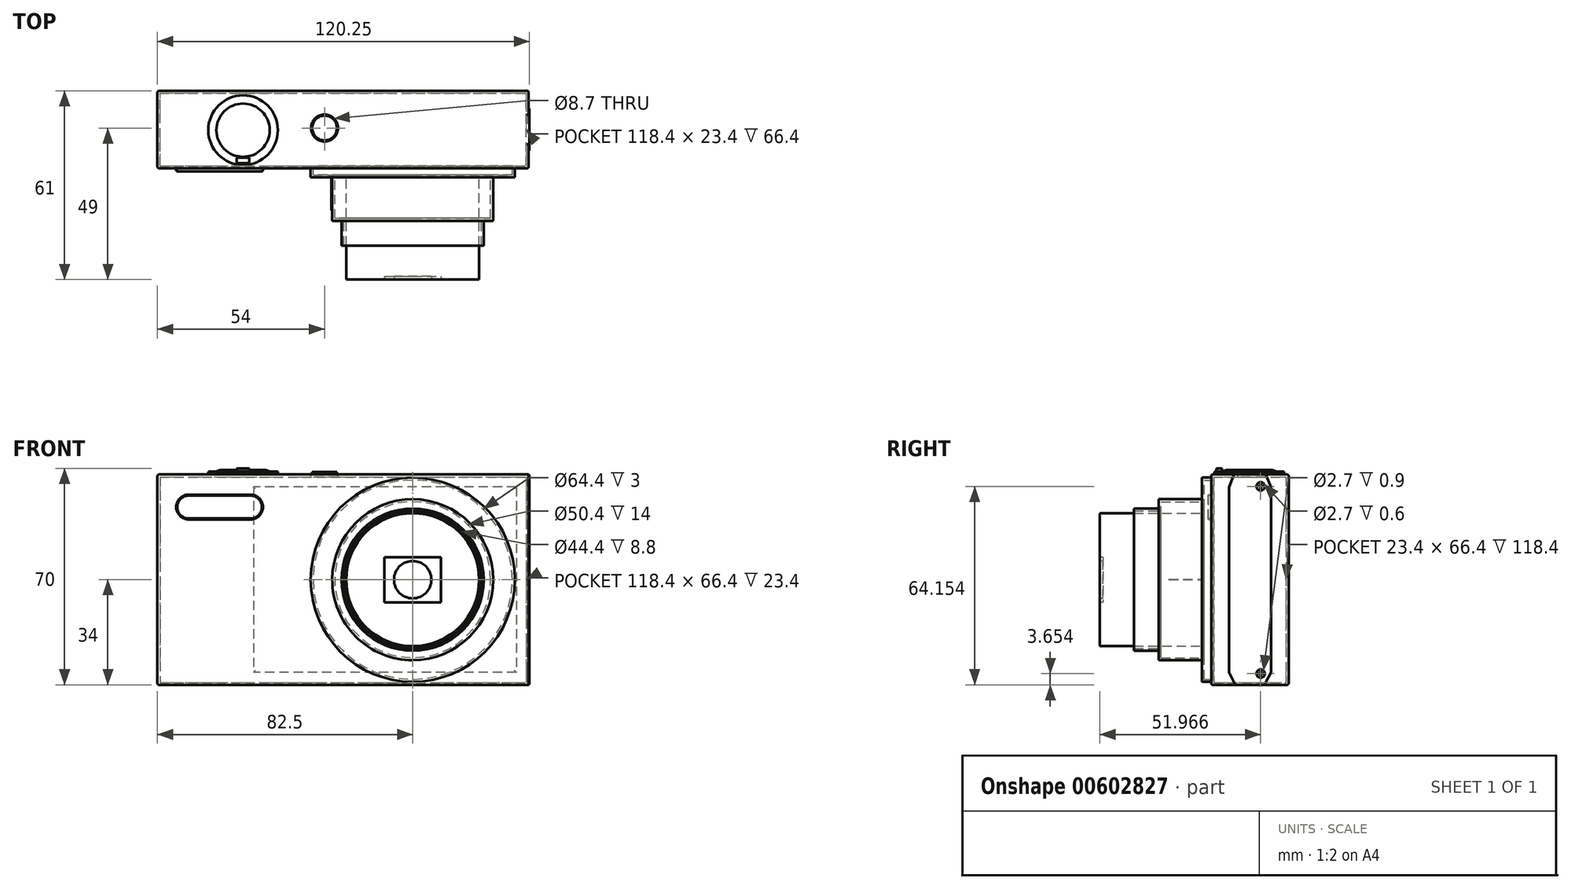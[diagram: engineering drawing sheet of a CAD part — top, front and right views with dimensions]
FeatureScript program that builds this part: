
annotation { "Feature Type Name" : "Feature", "Feature Type Description" : "" }
export const myFeature = defineFeature(function(context is Context, id is Id, definition is map)
    precondition{}
    {
        {
            var Q0;
            Q0=qCreatedBy(makeId("Front.planeOp"),FACE);
            var sketch = newSketch(context, id + "F0", { "sketchPlane" : qUnion([Q0])});
            skLineSegment(sketch, "E0.bottom", {"start": v(-60, 34) * mm, "end": v(60, 34) * mm});
            skLineSegment(sketch, "E0.top", {"start": v(-60, -34) * mm, "end": v(60, -34) * mm});
            skLineSegment(sketch, "E0.left", {"start": v(-60, 34) * mm, "end": v(-60, -34) * mm});
            skLineSegment(sketch, "E0.right", {"start": v(60, 34) * mm, "end": v(60, -34) * mm});
            skPoint(sketch, "E0.middle", {"position": v(0, 0) * mm});
            skCircle(sketch, "E1", {"center": v(22.5, 0) * mm, "radius": 33 * mm});
            skSolve(sketch);
        }
        {
            var Q0;
            Q0=makeQuery(id+"F0.imprint","IMPRINT",FACE,{"disambiguationData":[TD([[makeQuery(id+"F0.imprint","IMPRINT",EDGE,{"derivedFrom":sQuery(id+"F0.wireOp",EDGE,"E1")}),1.0]])]});
            extrude(context, id + "F1", {"entities" : qUnion([Q0]), "depth" : 28 * mm, "offsetDistance" : 25 * mm});
        }
        {
            var Q0;
            Q0=makeQuery(id+"F0.imprint","IMPRINT",FACE,{"disambiguationData":[TD([[makeQuery(id+"F0.imprint","IMPRINT",EDGE,{"derivedFrom":sQuery(id+"F0.wireOp",EDGE,"E0.bottom")}),-1.0]])]});
            extrude(context, id + "F2", {"entities" : qUnion([Q0]), "operationType" : NewBodyOperationType.ADD, "depth" : 25 * mm, "offsetDistance" : 25 * mm});
        }
        {
            var Q0;
            Q0=makeQuery(id+"F1.opExtrude","CAP_FACE",FACE,{"disambiguationData":[OSD([sQuery(id+"F0.wireOp",EDGE,"E1")])],"isStart":false});
            var sketch = newSketch(context, id + "F3", { "sketchPlane" : qUnion([Q0])});
            skCircle(sketch, "E2", {"center": v(22.5, 0) * mm, "radius": 26 * mm});
            skSolve(sketch);
        }
        {
            var Q0;
            Q0=makeQuery(id+"F3.imprint","IMPRINT",FACE,{"disambiguationData":[TD([[makeQuery(id+"F3.imprint","IMPRINT",EDGE,{"derivedFrom":sQuery(id+"F3.wireOp",EDGE,"E2")}),1.0]])]});
            var Q1;
            Q1=sQuery(id+"F3.wireOp",EDGE,"E2");
            extrude(context, id + "F4", {"entities" : qUnion([Q0]), "operationType" : NewBodyOperationType.ADD, "surfaceEntities" : qUnion([Q1]), "depth" : 14 * mm, "offsetDistance" : 25 * mm});
        }
        {
            var Q0;
            Q0=makeQuery(id+"F4.opExtrude","CAP_FACE",FACE,{"disambiguationData":[OSD([sQuery(id+"F3.wireOp",EDGE,"E2")])],"isStart":false});
            var sketch = newSketch(context, id + "F5", { "sketchPlane" : qUnion([Q0])});
            skCircle(sketch, "E3", {"center": v(22.5, 0) * mm, "radius": 23 * mm});
            skSolve(sketch);
        }
        {
            var Q0;
            Q0=makeQuery(id+"F5.imprint","IMPRINT",FACE,{"disambiguationData":[TD([[makeQuery(id+"F5.imprint","IMPRINT",EDGE,{"derivedFrom":sQuery(id+"F5.wireOp",EDGE,"E3")}),1.0]])]});
            extrude(context, id + "F6", {"entities" : qUnion([Q0]), "operationType" : NewBodyOperationType.ADD, "depth" : 8 * mm, "offsetDistance" : 25 * mm});
        }
        {
            var Q0;
            Q0=makeQuery(id+"F6.opExtrude","CAP_FACE",FACE,{"disambiguationData":[OSD([sQuery(id+"F5.wireOp",EDGE,"E3")])],"isStart":false});
            shell(context, id + "F7", {"entities" : qUnion([Q0]), "thickness" : 0.8 * mm});
        }
        {
            var Q0;
            Q0=qCreatedBy(makeId("Front.planeOp"),FACE);
            cPlane(context, id + "F8", {"entities" : qUnion([Q0]), "cplaneType" : CPlaneType.OFFSET, "offset" : 28 * mm, "width" : 150 * mm, "height" : 150 * mm});
        }
        {
            var Q0;
            Q0=qCreatedBy(id+"F8.planeOp",FACE);
            var sketch = newSketch(context, id + "F9", { "sketchPlane" : qUnion([Q0])});
            skCircle(sketch, "E4", {"center": v(22.5, 0) * mm, "radius": 21.5 * mm});
            skSolve(sketch);
        }
        {
            var Q0;
            Q0=makeQuery(id+"F9.imprint","IMPRINT",FACE,{"disambiguationData":[TD([[makeQuery(id+"F9.imprint","IMPRINT",EDGE,{"derivedFrom":sQuery(id+"F9.wireOp",EDGE,"E4")}),1.0]])]});
            extrude(context, id + "F10", {"entities" : qUnion([Q0]), "operationType" : NewBodyOperationType.ADD, "depth" : 33 * mm, "offsetDistance" : 25 * mm});
        }
        {
            var Q0;
            Q0=makeQuery(id+"F10.opExtrude","CAP_FACE",FACE,{"disambiguationData":[OSD([sQuery(id+"F9.wireOp",EDGE,"E4")])],"isStart":false});
            var sketch = newSketch(context, id + "F11", { "sketchPlane" : qUnion([Q0])});
            skLineSegment(sketch, "E5.bottom", {"start": v(13.35, 7.3) * mm, "end": v(31.65, 7.3) * mm});
            skLineSegment(sketch, "E5.top", {"start": v(13.35, -7.3) * mm, "end": v(31.65, -7.3) * mm});
            skLineSegment(sketch, "E5.left", {"start": v(13.35, 7.3) * mm, "end": v(13.35, -7.3) * mm});
            skLineSegment(sketch, "E5.right", {"start": v(31.65, 7.3) * mm, "end": v(31.65, -7.3) * mm});
            skPoint(sketch, "E5.middle", {"position": v(22.5, 0) * mm});
            skCircle(sketch, "E6", {"center": v(22.5, 0) * mm, "radius": 6.04 * mm});
            skSolve(sketch);
        }
        {
            var Q0;
            Q0=makeQuery(id+"F2.opExtrude","SWEPT_FACE",FACE,{"disambiguationData":[OSD([sQuery(id+"F0.wireOp",EDGE,"E0.bottom")])]});
            var sketch = newSketch(context, id + "F12", { "sketchPlane" : qUnion([Q0])});
            skCircle(sketch, "E7", {"center": v(-6, -12) * mm, "radius": 4 * mm});
            skCircle(sketch, "E8", {"center": v(-32.34, -12.7) * mm, "radius": 11.25 * mm});
            skCircle(sketch, "E9", {"center": v(-32.34, -12.7) * mm, "radius": 8.61 * mm});
            skPoint(sketch, "E10", {"position": v(-32.34, -22.45) * mm});
            skLineSegment(sketch, "E11.bottom", {"start": v(-30.34, -23.35) * mm, "end": v(-34.35, -23.35) * mm});
            skLineSegment(sketch, "E11.top", {"start": v(-30.34, -21.56) * mm, "end": v(-34.35, -21.56) * mm});
            skLineSegment(sketch, "E11.left", {"start": v(-30.34, -23.35) * mm, "end": v(-30.34, -21.56) * mm});
            skLineSegment(sketch, "E11.right", {"start": v(-34.35, -23.35) * mm, "end": v(-34.35, -21.56) * mm});
            skSolve(sketch);
        }
        {
            var Q0;
            Q0=makeQuery(id+"F12.imprint","IMPRINT",FACE,{"disambiguationData":[TD([[makeQuery(id+"F12.imprint","IMPRINT",EDGE,{"derivedFrom":sQuery(id+"F12.wireOp",EDGE,"E7")}),1.0]])]});
            extrude(context, id + "F13", {"entities" : qUnion([Q0]), "operationType" : NewBodyOperationType.ADD, "depth" : 0.75 * mm, "offsetDistance" : 25 * mm});
        }
        {
            var Q0;
            Q0=makeQuery(id+"F12.imprint","IMPRINT",FACE,{"disambiguationData":[TD([[makeQuery(id+"F12.imprint","IMPRINT",EDGE,{"derivedFrom":sQuery(id+"F12.wireOp",EDGE,"E11.bottom")}),-1.0]])]});
            extrude(context, id + "F14", {"entities" : qUnion([Q0]), "operationType" : NewBodyOperationType.ADD, "depth" : 2 * mm, "offsetDistance" : 25 * mm});
        }
        {
            var Q0;
            Q0=makeQuery(id+"F12.imprint","IMPRINT",FACE,{"disambiguationData":[TD([[makeQuery(id+"F12.imprint","IMPRINT",EDGE,{"derivedFrom":sQuery(id+"F12.wireOp",EDGE,"E8")}),1.0]])]});
            extrude(context, id + "F15", {"entities" : qUnion([Q0]), "operationType" : NewBodyOperationType.ADD, "depth" : 1 * mm, "offsetDistance" : 25 * mm});
        }
        {
            var Q0;
            Q0=makeQuery(id+"F12.imprint","IMPRINT",FACE,{"disambiguationData":[TD([[makeQuery(id+"F12.imprint","IMPRINT",EDGE,{"derivedFrom":sQuery(id+"F12.wireOp",EDGE,"E9")}),1.0]])]});
            extrude(context, id + "F16", {"entities" : qUnion([Q0]), "operationType" : NewBodyOperationType.ADD, "depth" : 1.5 * mm, "offsetDistance" : 25 * mm});
        }
        {
            var Q0;
            Q0=makeQuery(id+"F14.opExtrude","CAP_EDGE",EDGE,{"disambiguationData":[OSD([sQuery(id+"F12.wireOp",EDGE,"E11.bottom")])],"isStart":false});
            var Q1;
            Q1=makeQuery(id+"F14.opExtrude","CAP_EDGE",EDGE,{"disambiguationData":[OSD([sQuery(id+"F12.wireOp",EDGE,"E11.left")])],"isStart":false});
            var Q2;
            Q2=makeQuery(id+"F14.opExtrude","SWEPT_EDGE",EDGE,{"disambiguationData":[OSD([sQuery(id+"F12.wireOp",EDGE,"E11.bottom"),sQuery(id+"F12.wireOp",EDGE,"E11.left")])]});
            var Q3;
            Q3=makeQuery(id+"F14.opExtrude","CAP_EDGE",EDGE,{"disambiguationData":[OSD([sQuery(id+"F12.wireOp",EDGE,"E11.top")])],"isStart":false});
            var Q4;
            Q4=makeQuery(id+"F14.opExtrude","CAP_EDGE",EDGE,{"disambiguationData":[OSD([sQuery(id+"F12.wireOp",EDGE,"E11.right")])],"isStart":false});
            var Q5;
            Q5=makeQuery(id+"F14.opExtrude","SWEPT_EDGE",EDGE,{"disambiguationData":[OSD([sQuery(id+"F12.wireOp",EDGE,"E11.top"),sQuery(id+"F12.wireOp",EDGE,"E11.right")])]});
            var Q6;
            Q6=makeQuery(id+"F14.opExtrude","SWEPT_EDGE",EDGE,{"disambiguationData":[OSD([sQuery(id+"F12.wireOp",EDGE,"E11.top"),sQuery(id+"F12.wireOp",EDGE,"E11.left")])]});
            var Q7;
            Q7=makeQuery(id+"F14.opExtrude","SWEPT_EDGE",EDGE,{"disambiguationData":[OSD([sQuery(id+"F12.wireOp",EDGE,"E11.bottom"),sQuery(id+"F12.wireOp",EDGE,"E11.right")])]});
            var Q8;
            Q8=makeQuery(id+"F15.opExtrude","CAP_EDGE",EDGE,{"disambiguationData":[OSD([sQuery(id+"F12.wireOp",EDGE,"E11.bottom")])],"isStart":false});
            var Q9;
            Q9=makeQuery(id+"F15.opExtrude","CAP_EDGE",EDGE,{"disambiguationData":[OSD([sQuery(id+"F12.wireOp",EDGE,"E11.right")])],"isStart":false});
            fillet(context, id + "F17", {"entities" : qUnion([Q0, Q1, Q2, Q3, Q4, Q5, Q6, Q7, Q8, Q9]), "radius" : 0.2 * mm, "tangentPropagation" : true, "allowEdgeOverflow" : false});
        }
        {
            var Q0;
            Q0=makeQuery(id+"F16.opExtrude","CAP_EDGE",EDGE,{"disambiguationData":[OSD([sQuery(id+"F12.wireOp",EDGE,"E9")])],"isStart":false});
            fillet(context, id + "F18", {"entities" : qUnion([Q0]), "radius" : 5 * mm, "tangentPropagation" : true, "allowEdgeOverflow" : false});
        }
        {
            var Q0;
            Q0=makeQuery(id+"F12.imprint","IMPRINT",FACE,{"disambiguationData":[TD([[makeQuery(id+"F12.imprint","IMPRINT",EDGE,{"derivedFrom":sQuery(id+"F12.wireOp",EDGE,"E7")}),-1.0]])]});
            var sketch = newSketch(context, id + "F19", { "sketchPlane" : qUnion([Q0])});
            skCircle(sketch, "E12", {"center": v(-6, -12) * mm, "radius": 4.35 * mm});
            skSolve(sketch);
        }
        {
            var Q0;
            Q0 = qSketchRegion(id + "F19", true);
            extrude(context, id + "F20", {"entities" : qUnion([Q0]), "operationType" : NewBodyOperationType.REMOVE, "oppositeDirection" : true, "depth" : 1.5 * mm, "offsetDistance" : 25 * mm});
        }
        {
            var Q0;
            Q0=qCreatedBy(makeId("Top.planeOp"),FACE);
            var sketch = newSketch(context, id + "F21", { "sketchPlane" : qUnion([Q0])});
            skLineSegment(sketch, "E13", {"start": v(-3.5, -28) * mm, "end": v(-3.5, -38.66) * mm});
            skLineSegment(sketch, "E14", {"start": v(-3.77, -28) * mm, "end": v(-3.77, -38.66) * mm});
            skLineSegment(sketch, "E15", {"start": v(-3.77, -38.66) * mm, "end": v(-3.5, -38.66) * mm});
            skLineSegment(sketch, "E16", {"start": v(-3.77, -28) * mm, "end": v(-3.5, -28) * mm});
            skSolve(sketch);
        }
        {
            var Q0;
            Q0=makeQuery(id+"F21.imprint","IMPRINT",FACE,{"disambiguationData":[TD([[makeQuery(id+"F21.imprint","IMPRINT",EDGE,{"derivedFrom":sQuery(id+"F21.wireOp",EDGE,"E13")}),-1.0]])]});
            extrude(context, id + "F22", {"entities" : qUnion([Q0]), "operationType" : NewBodyOperationType.ADD, "depth" : .1 * mm, "offsetDistance" : 25 * mm});
        }
        {
            var Q0;
            Q0=makeQuery(id+"F2.opExtrude","SWEPT_FACE",FACE,{"disambiguationData":[OSD([sQuery(id+"F0.wireOp",EDGE,"E0.right")])]});
            var sketch = newSketch(context, id + "F23", { "sketchPlane" : qUnion([Q0])});
            skLineSegment(sketch, "E17", {"start": v(-12.5, 34) * mm, "end": v(-12.5, -34) * mm});
            skLineSegment(sketch, "E18", {"start": v(-17.62, 34) * mm, "end": v(-19.3, 29.83) * mm});
            skLineSegment(sketch, "E19", {"start": v(-19.3, 29.83) * mm, "end": v(-19.3, -30.02) * mm});
            skLineSegment(sketch, "E20", {"start": v(-19.3, -30.02) * mm, "end": v(-17.2, -34) * mm});
            skLineSegment(sketch, "E21.MirrorCS", {"start": v(-5.7, -30.02) * mm, "end": v(-7.8, -34) * mm});
            skLineSegment(sketch, "E22.MirrorCS", {"start": v(-7.38, 34) * mm, "end": v(-5.7, 29.83) * mm});
            skLineSegment(sketch, "E23.MirrorCS", {"start": v(-5.7, 29.83) * mm, "end": v(-5.7, -30.02) * mm});
            skSolve(sketch);
        }
        {
            var Q0;
            {var subQ2=sQuery(id+"F23.wireOp",EDGE,"E17");Q0=makeQuery(id+"F23.imprint","IMPRINT",FACE,{"disambiguationData":[TD([[makeQuery(id+"F23.imprint","IMPRINT",EDGE,{"derivedFrom":subQ2}),1.0]])]});}
            var Q1;
            {var subQ2=sQuery(id+"F23.wireOp",EDGE,"E17");Q1=makeQuery(id+"F23.imprint","IMPRINT",FACE,{"disambiguationData":[TD([[makeQuery(id+"F23.imprint","IMPRINT",EDGE,{"derivedFrom":subQ2}),-1.0]])]});}
            extrude(context, id + "F24", {"entities" : qUnion([Q0, Q1]), "operationType" : NewBodyOperationType.ADD, "depth" : .25 * mm, "offsetDistance" : 25 * mm});
        }
        {
            var Q0;
            Q0=makeQuery(id+"F24.opExtrude","CAP_FACE",FACE,{"disambiguationData":[OSD([sQuery(id+"F0.wireOp",EDGE,"E0.bottom"),sQuery(id+"F0.wireOp",EDGE,"E0.top"),sQuery(id+"F0.wireOp",EDGE,"E0.right"),sQuery(id+"F23.wireOp",EDGE,"E18"),sQuery(id+"F23.wireOp",EDGE,"E19"),sQuery(id+"F23.wireOp",EDGE,"E20"),sQuery(id+"F23.wireOp",EDGE,"E21.MirrorCS"),sQuery(id+"F23.wireOp",EDGE,"E22.MirrorCS"),sQuery(id+"F23.wireOp",EDGE,"E23.MirrorCS")])],"isStart":false});
            var sketch = newSketch(context, id + "F25", { "sketchPlane" : qUnion([Q0])});
            skCircle(sketch, "E24", {"center": v(-9.03, 30.15) * mm, "radius": 1.35 * mm});
            skCircle(sketch, "E25", {"center": v(-9.03, -30.35) * mm, "radius": 1.35 * mm});
            skSolve(sketch);
        }
        {
            var Q0;
            Q0=makeQuery(id+"F25.imprint","IMPRINT",FACE,{"disambiguationData":[TD([[makeQuery(id+"F25.imprint","IMPRINT",EDGE,{"derivedFrom":sQuery(id+"F25.wireOp",EDGE,"E24")}),1.0]])]});
            var Q1;
            Q1=makeQuery(id+"F25.imprint","IMPRINT",FACE,{"disambiguationData":[TD([[makeQuery(id+"F25.imprint","IMPRINT",EDGE,{"derivedFrom":sQuery(id+"F25.wireOp",EDGE,"E25")}),1.0]])]});
            var Q2;
            Q2=sQuery(id+"F25.wireOp",EDGE,"E24");
            var Q3;
            Q3=sQuery(id+"F25.wireOp",EDGE,"E25");
            extrude(context, id + "F26", {"entities" : qUnion([Q0, Q1]), "operationType" : NewBodyOperationType.REMOVE, "surfaceEntities" : qUnion([Q2, Q3]), "oppositeDirection" : true, "depth" : .3 * mm, "offsetDistance" : 25 * mm});
        }
        {
            var Q0;
            Q0=makeQuery(id+"F26.boolean.opBoolean","COPY",FACE,{"derivedFrom":makeQuery(id+"F26.opExtrude","CAP_FACE",FACE,{"disambiguationData":[OSD([sQuery(id+"F25.wireOp",EDGE,"E24")])],"isStart":false})});
            var sketch = newSketch(context, id + "F27", { "sketchPlane" : qUnion([Q0])});
            skLineSegment(sketch, "E26.bottom", {"start": v(-9.04, 31.5) * mm, "end": v(-8.98, 31.5) * mm});
            skLineSegment(sketch, "E26.top", {"start": v(-9.04, 28.8) * mm, "end": v(-8.98, 28.8) * mm});
            skLineSegment(sketch, "E26.left", {"start": v(-9.04, 31.5) * mm, "end": v(-9.04, 28.8) * mm});
            skLineSegment(sketch, "E26.right", {"start": v(-8.98, 31.5) * mm, "end": v(-8.98, 28.8) * mm});
            skLineSegment(sketch, "E27.bottom", {"start": v(-10.38, 30.24) * mm, "end": v(-7.69, 30.24) * mm});
            skLineSegment(sketch, "E27.top", {"start": v(-10.38, 30.18) * mm, "end": v(-7.69, 30.18) * mm});
            skLineSegment(sketch, "E27.left", {"start": v(-10.38, 30.24) * mm, "end": v(-10.38, 30.18) * mm});
            skLineSegment(sketch, "E27.right", {"start": v(-7.69, 30.24) * mm, "end": v(-7.69, 30.18) * mm});
            skSolve(sketch);
        }
        {
            var Q0;
            Q0=makeQuery(id+"F26.boolean.opBoolean","COPY",FACE,{"derivedFrom":makeQuery(id+"F26.opExtrude","CAP_FACE",FACE,{"disambiguationData":[OSD([sQuery(id+"F25.wireOp",EDGE,"E25")])],"isStart":false})});
            extrude(context, id + "F28", {"entities" : qUnion([Q0]), "operationType" : NewBodyOperationType.REMOVE, "oppositeDirection" : true, "depth" : .3 * mm, "offsetDistance" : 25 * mm});
        }
        {
            var Q0;
            Q0=makeQuery(id+"F28.boolean.opBoolean","COPY",FACE,{"derivedFrom":makeQuery(id+"F28.opExtrude","CAP_FACE",FACE,{"disambiguationData":[OSD([sQuery(id+"F25.wireOp",EDGE,"E25")])],"isStart":false})});
            var sketch = newSketch(context, id + "F29", { "sketchPlane" : qUnion([Q0])});
            skLineSegment(sketch, "E28.bottom", {"start": v(-9.07, -29) * mm, "end": v(-9.01, -29) * mm});
            skLineSegment(sketch, "E28.top", {"start": v(-9.07, -31.7) * mm, "end": v(-9.01, -31.7) * mm});
            skLineSegment(sketch, "E28.left", {"start": v(-9.07, -29) * mm, "end": v(-9.07, -31.7) * mm});
            skLineSegment(sketch, "E28.right", {"start": v(-9.01, -29) * mm, "end": v(-9.01, -31.7) * mm});
            skPoint(sketch, "E29.oppositeSnap0", {"position": v(-9.07, -30.35) * mm});
            skLineSegment(sketch, "E29.bottom", {"start": v(-10.38, -30.29) * mm, "end": v(-7.68, -30.29) * mm});
            skLineSegment(sketch, "E29.top", {"start": v(-10.38, -30.35) * mm, "end": v(-7.68, -30.35) * mm});
            skLineSegment(sketch, "E29.left", {"start": v(-10.38, -30.29) * mm, "end": v(-10.38, -30.35) * mm});
            skLineSegment(sketch, "E29.right", {"start": v(-7.68, -30.29) * mm, "end": v(-7.68, -30.35) * mm});
            skSolve(sketch);
        }
        {
            var Q0;
            {var subQ0=sQuery(id+"F29.wireOp",EDGE,"E28.bottom");Q0=makeQuery(id+"F29.imprint","IMPRINT",FACE,{"disambiguationData":[TD([[makeQuery(id+"F29.imprint","IMPRINT",EDGE,{"derivedFrom":subQ0}),-1.0]])]});}
            var Q1;
            {var subQ4=sQuery(id+"F29.wireOp",EDGE,"E29.top");var subQ6=sQuery(id+"F29.wireOp",EDGE,"E28.left");var subQ7=makeQuery(id+"F29.imprint","INTERSECT",VERTEX,{"derivedFrom":[subQ6,subQ4]});Q1=makeQuery(id+"F29.imprint","IMPRINT",FACE,{"disambiguationData":[TD([[makeQuery(id+"F29.imprint","IMPRINT",EDGE,{"disambiguationData":[TD([[subQ7,-1.0]])],"derivedFrom":subQ6}),1.0]])]});}
            var Q2;
            {var subQ0=sQuery(id+"F29.wireOp",EDGE,"E29.bottom");var subQ1=sQuery(id+"F29.wireOp",EDGE,"E28.left");var subQ2=makeQuery(id+"F29.imprint","INTERSECT",VERTEX,{"derivedFrom":[subQ1,subQ0]});Q2=makeQuery(id+"F29.imprint","IMPRINT",FACE,{"disambiguationData":[TD([[makeQuery(id+"F29.imprint","IMPRINT",EDGE,{"disambiguationData":[TD([[subQ2,-1.0]])],"derivedFrom":subQ1}),1.0]])]});}
            var Q3;
            {var subQ5=sQuery(id+"F29.wireOp",EDGE,"E29.bottom");var subQ6=sQuery(id+"F29.wireOp",EDGE,"E28.right");var subQ7=makeQuery(id+"F29.imprint","INTERSECT",VERTEX,{"derivedFrom":[subQ6,subQ5]});Q3=makeQuery(id+"F29.imprint","IMPRINT",FACE,{"disambiguationData":[TD([[makeQuery(id+"F29.imprint","IMPRINT",EDGE,{"disambiguationData":[TD([[subQ7,-1.0]])],"derivedFrom":subQ6}),1.0]])]});}
            var Q4;
            {var subQ5=sQuery(id+"F29.wireOp",EDGE,"E29.left");Q4=makeQuery(id+"F29.imprint","IMPRINT",FACE,{"disambiguationData":[TD([[makeQuery(id+"F29.imprint","IMPRINT",EDGE,{"derivedFrom":subQ5}),1.0]])]});}
            var Q5;
            Q5=sQuery(id+"F29.wireOp",EDGE,"E28.left");
            var Q6;
            Q6=sQuery(id+"F29.wireOp",EDGE,"E28.right");
            extrude(context, id + "F30", {"entities" : qUnion([Q0, Q1, Q2, Q3, Q4]), "operationType" : NewBodyOperationType.REMOVE, "surfaceEntities" : qUnion([Q5, Q6]), "oppositeDirection" : true, "depth" : .3 * mm, "offsetDistance" : 25 * mm});
        }
        {
            var Q0;
            {var subQ0=sQuery(id+"F27.wireOp",EDGE,"E27.bottom");var subQ1=sQuery(id+"F27.wireOp",EDGE,"E26.right");var subQ2=makeQuery(id+"F27.imprint","INTERSECT",VERTEX,{"derivedFrom":[subQ1,subQ0]});Q0=makeQuery(id+"F27.imprint","IMPRINT",FACE,{"disambiguationData":[TD([[makeQuery(id+"F27.imprint","IMPRINT",EDGE,{"disambiguationData":[TD([[subQ2,1.0]])],"derivedFrom":subQ1}),-1.0]])]});}
            var Q1;
            {var subQ0=sQuery(id+"F27.wireOp",EDGE,"E27.bottom");var subQ1=sQuery(id+"F27.wireOp",EDGE,"E26.left");var subQ2=makeQuery(id+"F27.imprint","INTERSECT",VERTEX,{"derivedFrom":[subQ1,subQ0]});Q1=makeQuery(id+"F27.imprint","IMPRINT",FACE,{"disambiguationData":[TD([[makeQuery(id+"F27.imprint","IMPRINT",EDGE,{"disambiguationData":[TD([[subQ2,-1.0]])],"derivedFrom":subQ1}),1.0]])]});}
            var Q2;
            {var subQ5=sQuery(id+"F27.wireOp",EDGE,"E27.right");Q2=makeQuery(id+"F27.imprint","IMPRINT",FACE,{"disambiguationData":[TD([[makeQuery(id+"F27.imprint","IMPRINT",EDGE,{"derivedFrom":subQ5}),-1.0]])]});}
            var Q3;
            {var subQ5=sQuery(id+"F27.wireOp",EDGE,"E27.left");Q3=makeQuery(id+"F27.imprint","IMPRINT",FACE,{"disambiguationData":[TD([[makeQuery(id+"F27.imprint","IMPRINT",EDGE,{"derivedFrom":subQ5}),1.0]])]});}
            var Q4;
            {var subQ0=sQuery(id+"F27.wireOp",EDGE,"E26.top");Q4=makeQuery(id+"F27.imprint","IMPRINT",FACE,{"disambiguationData":[TD([[makeQuery(id+"F27.imprint","IMPRINT",EDGE,{"derivedFrom":subQ0}),1.0]])]});}
            extrude(context, id + "F31", {"entities" : qUnion([Q0, Q1, Q2, Q3, Q4]), "operationType" : NewBodyOperationType.REMOVE, "oppositeDirection" : true, "depth" : .3 * mm, "offsetDistance" : 25 * mm});
        }
        {
            var Q0;
            Q0=makeQuery(id+"F2.opExtrude","SWEPT_FACE",FACE,{"disambiguationData":[OSD([sQuery(id+"F0.wireOp",EDGE,"E0.left")])]});
            fillet(context, id + "F32", {"entities" : qUnion([Q0]), "radius" : .5 * mm, "tangentPropagation" : true, "allowEdgeOverflow" : false});
        }
        {
            var Q0;
            {var subQ0=sQuery(id+"F0.wireOp",EDGE,"E0.right");var subQ1=sQuery(id+"F0.wireOp",EDGE,"E0.bottom");var subQ3=sQuery(id+"F0.wireOp",EDGE,"E1");Q0=makeQuery(id+"F24.boolean.opBoolean","MERGE",FACE,{"derivedFrom":[makeQuery(id+"F15.boolean.opBoolean","SPLIT",FACE,{"disambiguationData":[TD([makeQuery(id+"F1.opExtrude","CAP_FACE",FACE,{"disambiguationData":[OSD([subQ3])],"isStart":true})])],"derivedFrom":makeQuery(id+"F2.opExtrude","SWEPT_FACE",FACE,{"disambiguationData":[OSD([subQ1])]})}),makeQuery(id+"F24.opExtrude","SWEPT_FACE",FACE,{"disambiguationData":[OSD([subQ1,subQ0])]})]});}
            fillet(context, id + "F33", {"entities" : qUnion([Q0]), "radius" : .5 * mm, "tangentPropagation" : true, "allowEdgeOverflow" : false});
        }
        {
            var Q0;
            Q0=makeQuery(id+"F2.opExtrude","CAP_EDGE",EDGE,{"disambiguationData":[OSD([sQuery(id+"F0.wireOp",EDGE,"E0.right")])],"isStart":false});
            var Q1;
            Q1=makeQuery(id+"F24.opExtrude","CAP_EDGE",EDGE,{"disambiguationData":[OSD([sQuery(id+"F0.wireOp",EDGE,"E0.top"),sQuery(id+"F0.wireOp",EDGE,"E0.right")])],"isStart":false});
            var Q2;
            Q2=makeQuery(id+"F2.opExtrude","CAP_EDGE",EDGE,{"disambiguationData":[OSD([sQuery(id+"F0.wireOp",EDGE,"E0.right")])],"isStart":true});
            var Q3;
            {var subQ1=sQuery(id+"F0.wireOp",EDGE,"E1");var subQ2=sQuery(id+"F0.wireOp",EDGE,"E0.right");var subQ3=sQuery(id+"F0.wireOp",EDGE,"E0.bottom");var subQ6=makeQuery(id+"F1.opExtrude","CAP_FACE",FACE,{"disambiguationData":[OSD([subQ1])],"isStart":true});var subQ9=makeQuery(id+"F2.opExtrude","SWEPT_FACE",FACE,{"disambiguationData":[OSD([subQ2])]});Q3=makeQuery(id+"F33.opFillet","BLEND_EDGE",EDGE,{"blendedFrom":[makeQuery(id+"F24.boolean.opBoolean","SPLIT",EDGE,{"disambiguationData":[TD([subQ6])],"derivedFrom":makeQuery(id+"F2.opExtrude","SWEPT_EDGE",EDGE,{"disambiguationData":[OSD([subQ3,subQ2])]})}),makeQuery(id+"F24.boolean.opBoolean","SPLIT",FACE,{"disambiguationData":[TD([subQ6])],"derivedFrom":subQ9})],"blendedInto":[makeQuery(id+"F24.boolean.opBoolean","SPLIT",FACE,{"disambiguationData":[TD([subQ6])],"derivedFrom":subQ9})]});}
            var Q4;
            {var subQ0=sQuery(id+"F0.wireOp",EDGE,"E0.right");var subQ1=sQuery(id+"F0.wireOp",EDGE,"E0.bottom");Q4=makeQuery(id+"F33.opFillet","BLEND_EDGE",EDGE,{"blendedFrom":[makeQuery(id+"F24.opExtrude","CAP_EDGE",EDGE,{"disambiguationData":[OSD([subQ1,subQ0])],"isStart":false}),makeQuery(id+"F24.opExtrude","CAP_FACE",FACE,{"disambiguationData":[OSD([subQ1,sQuery(id+"F0.wireOp",EDGE,"E0.top"),subQ0,sQuery(id+"F23.wireOp",EDGE,"E18"),sQuery(id+"F23.wireOp",EDGE,"E19"),sQuery(id+"F23.wireOp",EDGE,"E20"),sQuery(id+"F23.wireOp",EDGE,"E21.MirrorCS"),sQuery(id+"F23.wireOp",EDGE,"E22.MirrorCS"),sQuery(id+"F23.wireOp",EDGE,"E23.MirrorCS")])],"isStart":false})],"blendedInto":[makeQuery(id+"F24.opExtrude","CAP_FACE",FACE,{"disambiguationData":[OSD([subQ1,sQuery(id+"F0.wireOp",EDGE,"E0.top"),subQ0,sQuery(id+"F23.wireOp",EDGE,"E18"),sQuery(id+"F23.wireOp",EDGE,"E19"),sQuery(id+"F23.wireOp",EDGE,"E20"),sQuery(id+"F23.wireOp",EDGE,"E21.MirrorCS"),sQuery(id+"F23.wireOp",EDGE,"E22.MirrorCS"),sQuery(id+"F23.wireOp",EDGE,"E23.MirrorCS")])],"isStart":false})]});}
            var Q5;
            {var subQ0=makeQuery(id+"F24.opExtrude","SWEPT_FACE",FACE,{"disambiguationData":[OSD([sQuery(id+"F23.wireOp",EDGE,"E18")])]});var subQ2=sQuery(id+"F0.wireOp",EDGE,"E0.right");var subQ3=sQuery(id+"F0.wireOp",EDGE,"E0.bottom");var subQ7=makeQuery(id+"F2.opExtrude","SWEPT_FACE",FACE,{"disambiguationData":[OSD([subQ2])]});Q5=makeQuery(id+"F33.opFillet","BLEND_EDGE",EDGE,{"blendedFrom":[makeQuery(id+"F24.boolean.opBoolean","SPLIT",EDGE,{"disambiguationData":[TD([subQ0])],"derivedFrom":makeQuery(id+"F2.opExtrude","SWEPT_EDGE",EDGE,{"disambiguationData":[OSD([subQ3,subQ2])]})}),makeQuery(id+"F24.boolean.opBoolean","SPLIT",FACE,{"disambiguationData":[TD([subQ0])],"derivedFrom":subQ7})],"blendedInto":[makeQuery(id+"F24.boolean.opBoolean","SPLIT",FACE,{"disambiguationData":[TD([subQ0])],"derivedFrom":subQ7})]});}
            fillet(context, id + "F34", {"entities" : qUnion([Q0, Q1, Q2, Q3, Q4, Q5]), "radius" : .5 * mm, "tangentPropagation" : true, "allowEdgeOverflow" : false});
        }
        {
            var Q0;
            Q0=makeQuery(id+"F11.imprint","IMPRINT",FACE,{"disambiguationData":[TD([[makeQuery(id+"F11.imprint","IMPRINT",EDGE,{"derivedFrom":sQuery(id+"F11.wireOp",EDGE,"E5.bottom")}),-1.0]])]});
            extrude(context, id + "F35", {"entities" : qUnion([Q0]), "operationType" : NewBodyOperationType.REMOVE, "oppositeDirection" : true, "depth" : 1 * mm, "offsetDistance" : 25 * mm});
        }
        {
            var Q0;
            {var subQ0=sQuery(id+"F0.wireOp",EDGE,"E0.top");Q0=makeQuery(id+"F24.boolean.opBoolean","MERGE",FACE,{"derivedFrom":[makeQuery(id+"F2.opExtrude","SWEPT_FACE",FACE,{"disambiguationData":[OSD([subQ0])]}),makeQuery(id+"F24.opExtrude","SWEPT_FACE",FACE,{"disambiguationData":[OSD([subQ0,sQuery(id+"F0.wireOp",EDGE,"E0.right")])]})]});}
            fillet(context, id + "F36", {"entities" : qUnion([Q0]), "radius" : .5 * mm, "tangentPropagation" : true, "allowEdgeOverflow" : false});
        }
        {
            var Q0;
            Q0=makeQuery(id+"F2.opExtrude","CAP_FACE",FACE,{"disambiguationData":[OSD([sQuery(id+"F0.wireOp",EDGE,"E0.bottom"),sQuery(id+"F0.wireOp",EDGE,"E0.top"),sQuery(id+"F0.wireOp",EDGE,"E0.left"),sQuery(id+"F0.wireOp",EDGE,"E0.right"),sQuery(id+"F0.wireOp",EDGE,"E1")])],"isStart":false});
            var sketch = newSketch(context, id + "F37", { "sketchPlane" : qUnion([Q0])});
            skArc(sketch, "E30", {"start": v(-49.92, 27.47) * mm, "mid": v(-53.92, 23.47) * mm, "end": v(-49.92, 19.47) * mm});
            skArc(sketch, "E31", {"start": v(-29.92, 19.48) * mm, "mid": v(-25.92, 23.48) * mm, "end": v(-29.92, 27.48) * mm});
            skLineSegment(sketch, "E32", {"start": v(-49.92, 27.47) * mm, "end": v(-29.92, 27.48) * mm});
            skLineSegment(sketch, "E33", {"start": v(-49.92, 19.47) * mm, "end": v(-29.92, 19.48) * mm});
            skSolve(sketch);
        }
        {
            var Q0;
            Q0=makeQuery(id+"F37.imprint","IMPRINT",FACE,{"disambiguationData":[TD([[makeQuery(id+"F37.imprint","IMPRINT",EDGE,{"derivedFrom":sQuery(id+"F37.wireOp",EDGE,"E30")}),1.0]])]});
            extrude(context, id + "F38", {"entities" : qUnion([Q0]), "operationType" : NewBodyOperationType.ADD, "depth" : 1 * mm, "offsetDistance" : 25 * mm});
        }
        {
            var Q0;
            Q0=makeQuery(id+"F38.opExtrude","CAP_FACE",FACE,{"disambiguationData":[OSD([sQuery(id+"F37.wireOp",EDGE,"E30"),sQuery(id+"F37.wireOp",EDGE,"E31"),sQuery(id+"F37.wireOp",EDGE,"E32"),sQuery(id+"F37.wireOp",EDGE,"E33")])],"isStart":false});
            fillet(context, id + "F39", {"entities" : qUnion([Q0]), "radius" : .3 * mm, "tangentPropagation" : true, "allowEdgeOverflow" : false});
        }
        {
            var Q0;
            Q0=makeQuery(id+"F38.opExtrude","CAP_FACE",FACE,{"disambiguationData":[OSD([sQuery(id+"F37.wireOp",EDGE,"E30"),sQuery(id+"F37.wireOp",EDGE,"E31"),sQuery(id+"F37.wireOp",EDGE,"E32"),sQuery(id+"F37.wireOp",EDGE,"E33")])],"isStart":false});
            extrude(context, id + "F40", {"entities" : qUnion([Q0]), "operationType" : NewBodyOperationType.REMOVE, "oppositeDirection" : true, "depth" : 1 * mm, "offsetDistance" : 25 * mm});
        }
        {
            var Q0;
            Q0=makeQuery(id+"F0.imprint","IMPRINT",FACE,{"disambiguationData":[TD([[makeQuery(id+"F0.imprint","IMPRINT",EDGE,{"derivedFrom":sQuery(id+"F0.wireOp",EDGE,"E0.bottom")}),-1.0]])]});
            var sketch = newSketch(context, id + "F41", { "sketchPlane" : qUnion([Q0])});
            skLineSegment(sketch, "E34.bottom", {"start": v(56, 30) * mm, "end": v(-29, 30) * mm});
            skLineSegment(sketch, "E34.top", {"start": v(56, -30) * mm, "end": v(-29, -30) * mm});
            skLineSegment(sketch, "E34.left", {"start": v(56, 30) * mm, "end": v(56, -30) * mm});
            skLineSegment(sketch, "E34.right", {"start": v(-29, 30) * mm, "end": v(-29, -30) * mm});
            skSolve(sketch);
        }
        {
            var Q0;
            {var subQ0=sQuery(id+"F41.wireOp",EDGE,"E34.right");Q0=makeQuery(id+"F41.imprint","IMPRINT",FACE,{"disambiguationData":[TD([[makeQuery(id+"F41.imprint","IMPRINT",EDGE,{"derivedFrom":subQ0}),1.0]])]});}
            var Q1;
            {var subQ0=sQuery(id+"F41.wireOp",EDGE,"E34.left");Q1=makeQuery(id+"F41.imprint","IMPRINT",FACE,{"disambiguationData":[TD([[makeQuery(id+"F41.imprint","IMPRINT",EDGE,{"derivedFrom":subQ0}),-1.0]])]});}
            var Q2;
            {var subQ0=sQuery(id+"F41.wireOp",EDGE,"E34.bottom");var subQ1=makeQuery(id+"F0.imprint","IMPRINT",EDGE,{"derivedFrom":sQuery(id+"F0.wireOp",EDGE,"E1")});var subQ2=makeQuery(id+"F41.imprint","INTERSECT",VERTEX,{"disambiguationData":[OD(0.0)],"derivedFrom":[subQ1,subQ0]});Q2=makeQuery(id+"F41.imprint","IMPRINT",FACE,{"disambiguationData":[TD([[makeQuery(id+"F41.imprint","IMPRINT",EDGE,{"disambiguationData":[TD([[subQ2,-1.0]])],"derivedFrom":subQ0}),1.0]])]});}
            var Q3;
            Q3=sQuery(id+"F41.wireOp",EDGE,"E34.right");
            var Q4;
            Q4=sQuery(id+"F41.wireOp",EDGE,"E34.bottom");
            var Q5;
            Q5=sQuery(id+"F41.wireOp",EDGE,"E34.top");
            var Q6;
            Q6=sQuery(id+"F41.wireOp",EDGE,"E34.left");
            extrude(context, id + "F42", {"entities" : qUnion([Q0, Q1, Q2]), "operationType" : NewBodyOperationType.REMOVE, "surfaceEntities" : qUnion([Q3, Q4, Q5, Q6]), "depth" : 0.1 * mm, "offsetDistance" : 25 * mm});
        }
        {
            var Q0;
            Q0=makeQuery(id+"F42.boolean.opBoolean","COPY",FACE,{"derivedFrom":makeQuery(id+"F42.opExtrude","CAP_FACE",FACE,{"disambiguationData":[OSD([sQuery(id+"F41.wireOp",EDGE,"E34.bottom"),sQuery(id+"F41.wireOp",EDGE,"E34.top"),sQuery(id+"F41.wireOp",EDGE,"E34.left"),sQuery(id+"F41.wireOp",EDGE,"E34.right")])],"isStart":false})});
            fillet(context, id + "F43", {"entities" : qUnion([Q0]), "radius" : 2 * mm, "tangentPropagation" : true, "allowEdgeOverflow" : false});
        }
    });
